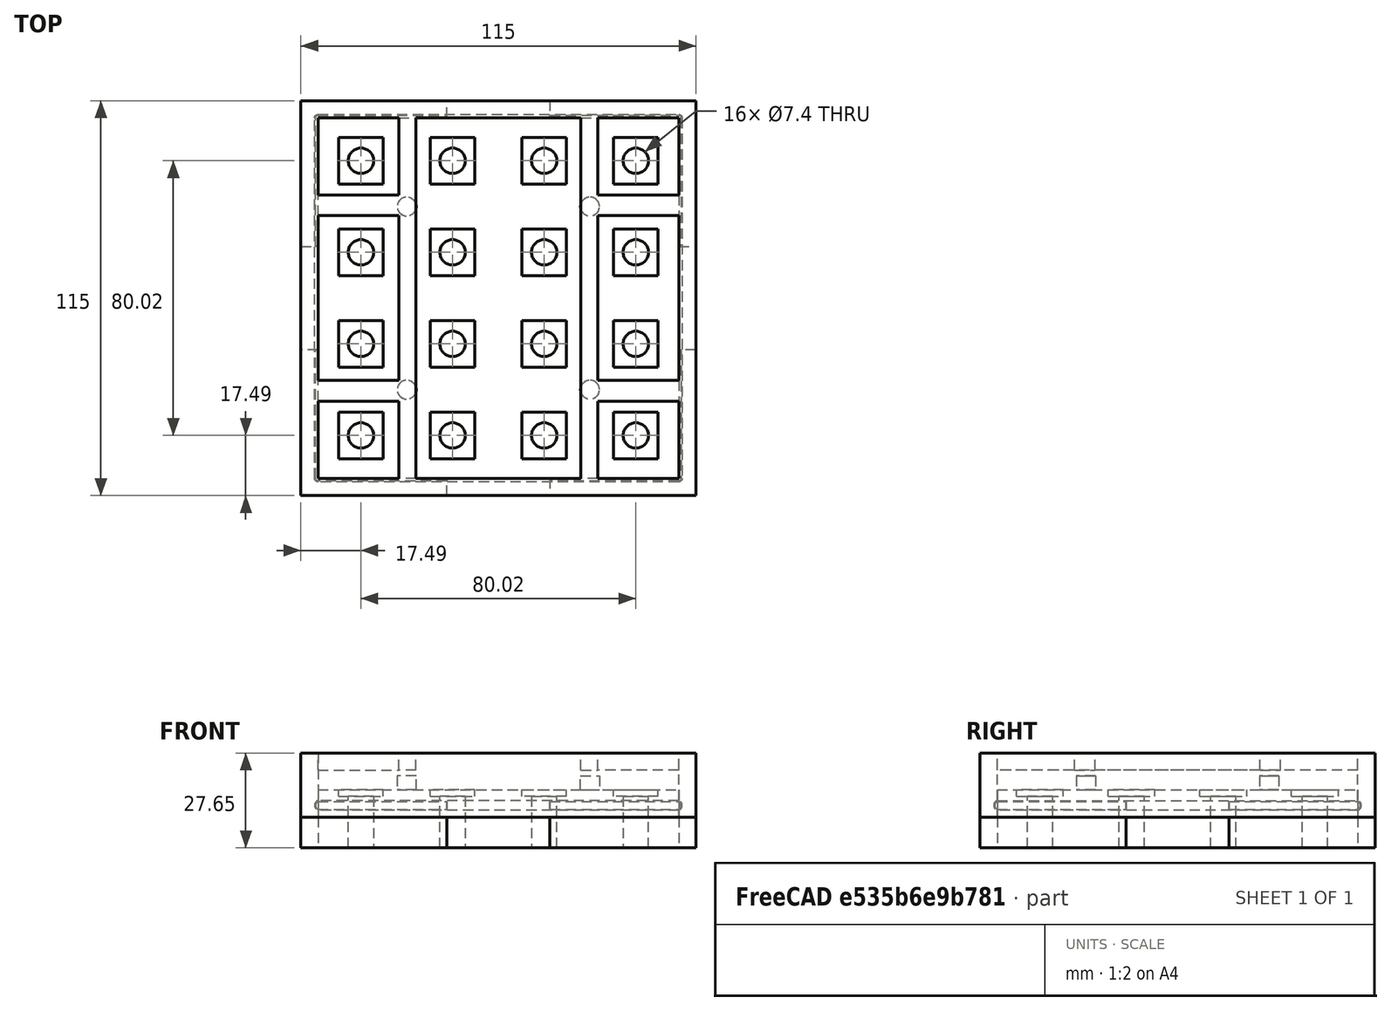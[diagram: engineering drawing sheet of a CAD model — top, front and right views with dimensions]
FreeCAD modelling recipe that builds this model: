
FCSTD DOCUMENT  (FreeCAD 0.21R33668 +26 (Git))
Label: EN16_solder_jig másolata
License: All rights reserved
LicenseURL: https://en.wikipedia.org/wiki/All_rights_reserved
objects: Sketcher::SketchObject×11, PartDesign::Pad×4, PartDesign::Pocket×4, PartDesign::Plane×2, PartDesign::Mirrored×2, PartDesign::Body×2, PartDesign::AdditivePipe×1, PartDesign::SubtractivePipe×1, PartDesign::PolarPattern×1
note: 38 computed .brp shape members not serialized (recipe doc carries the construction recipe); baked Part::Feature solids carry a one-line shape summary decoded from their .brp

FEATURE [Sketcher::SketchObject] Sketch
  FullyConstrained = true
  MapMode = 5
  Support = -> [XY_Plane]
  sketch-geometry (48):
    g0: LineSegment StartX=-46.51 StartY=46.81 StartZ=0 EndX=-46.51 EndY=33.21 EndZ=0
    g1: LineSegment StartX=-46.51 StartY=33.21 StartZ=0 EndX=-33.51 EndY=33.21 EndZ=0
    g2: LineSegment StartX=-33.51 StartY=33.21 StartZ=0 EndX=-33.51 EndY=46.81 EndZ=0
    g3: LineSegment StartX=-33.51 StartY=46.81 StartZ=0 EndX=-46.51 EndY=46.81 EndZ=0
    g4: GeomPoint X=-40.01 Y=40.01 Z=0
    g5: LineSegment StartX=-19.84 StartY=46.81 StartZ=0 EndX=-19.84 EndY=33.21 EndZ=0
    g6: LineSegment StartX=-19.84 StartY=33.21 StartZ=0 EndX=-6.84 EndY=33.21 EndZ=0
    g7: LineSegment StartX=-6.84 StartY=33.21 StartZ=0 EndX=-6.84 EndY=46.81 EndZ=0
    g8: LineSegment StartX=-6.84 StartY=46.81 StartZ=0 EndX=-19.84 EndY=46.81 EndZ=0
    g9: GeomPoint X=-13.34 Y=40.01 Z=0
    g10: LineSegment StartX=-46.51 StartY=20.14 StartZ=0 EndX=-46.51 EndY=6.54 EndZ=0
    g11: LineSegment StartX=-46.51 StartY=6.54 StartZ=0 EndX=-33.51 EndY=6.54 EndZ=0
    g12: LineSegment StartX=-33.51 StartY=6.54 StartZ=0 EndX=-33.51 EndY=20.14 EndZ=0
    g13: LineSegment StartX=-33.51 StartY=20.14 StartZ=0 EndX=-46.51 EndY=20.14 EndZ=0
    g14: GeomPoint X=-40.01 Y=13.34 Z=0
    g15: LineSegment StartX=-19.84 StartY=20.14 StartZ=0 EndX=-19.84 EndY=6.54 EndZ=0
    g16: LineSegment StartX=-19.84 StartY=6.54 StartZ=0 EndX=-6.84 EndY=6.54 EndZ=0
    g17: LineSegment StartX=-6.84 StartY=6.54 StartZ=0 EndX=-6.84 EndY=20.14 EndZ=0
    g18: LineSegment StartX=-6.84 StartY=20.14 StartZ=0 EndX=-19.84 EndY=20.14 EndZ=0
    g19: GeomPoint X=-13.34 Y=13.34 Z=0
    g20: LineSegment StartX=-46.51 StartY=-46.81 StartZ=0 EndX=-46.51 EndY=-33.21 EndZ=0
    g21: LineSegment StartX=-46.51 StartY=-33.21 StartZ=0 EndX=-33.51 EndY=-33.21 EndZ=0
    g22: LineSegment StartX=-33.51 StartY=-33.21 StartZ=0 EndX=-33.51 EndY=-46.81 EndZ=0
    g23: LineSegment StartX=-33.51 StartY=-46.81 StartZ=0 EndX=-46.51 EndY=-46.81 EndZ=0
    g24: GeomPoint X=-40.01 Y=-40.01 Z=0
    g25: LineSegment StartX=-19.84 StartY=-46.81 StartZ=0 EndX=-19.84 EndY=-33.21 EndZ=0
    g26: LineSegment StartX=-19.84 StartY=-33.21 StartZ=0 EndX=-6.84 EndY=-33.21 EndZ=0
    g27: LineSegment StartX=-6.84 StartY=-33.21 StartZ=0 EndX=-6.84 EndY=-46.81 EndZ=0
    g28: LineSegment StartX=-6.84 StartY=-46.81 StartZ=0 EndX=-19.84 EndY=-46.81 EndZ=0
    g29: GeomPoint X=-13.34 Y=-40.01 Z=0
    g30: LineSegment StartX=-46.51 StartY=-20.14 StartZ=0 EndX=-46.51 EndY=-6.54 EndZ=0
    g31: LineSegment StartX=-46.51 StartY=-6.54 StartZ=0 EndX=-33.51 EndY=-6.54 EndZ=0
    g32: LineSegment StartX=-33.51 StartY=-6.54 StartZ=0 EndX=-33.51 EndY=-20.14 EndZ=0
    g33: LineSegment StartX=-33.51 StartY=-20.14 StartZ=0 EndX=-46.51 EndY=-20.14 EndZ=0
    g34: GeomPoint X=-40.01 Y=-13.34 Z=0
    g35: LineSegment StartX=-19.84 StartY=-20.14 StartZ=0 EndX=-19.84 EndY=-6.54 EndZ=0
    g36: LineSegment StartX=-19.84 StartY=-6.54 StartZ=0 EndX=-6.84 EndY=-6.54 EndZ=0
    g37: LineSegment StartX=-6.84 StartY=-6.54 StartZ=0 EndX=-6.84 EndY=-20.14 EndZ=0
    g38: LineSegment StartX=-6.84 StartY=-20.14 StartZ=0 EndX=-19.84 EndY=-20.14 EndZ=0
    g39: GeomPoint X=-13.34 Y=-13.34 Z=0
    g40: LineSegment StartX=-40.01 StartY=40.01 StartZ=0 EndX=-13.34 EndY=40.01 EndZ=0
    g41: LineSegment StartX=-13.34 StartY=40.01 StartZ=0 EndX=-13.34 EndY=13.34 EndZ=0
    g42: LineSegment StartX=-13.34 StartY=13.34 StartZ=0 EndX=-13.34 EndY=0 EndZ=0
    g43: LineSegment StartX=-13.34 StartY=0 StartZ=0 EndX=-13.34 EndY=-13.34 EndZ=0
    g44: LineSegment StartX=-13.34 StartY=-13.34 StartZ=0 EndX=-13.34 EndY=-40.01 EndZ=0
    g45: LineSegment StartX=-13.34 StartY=-13.34 StartZ=0 EndX=-40.01 EndY=-13.34 EndZ=0
    g46: LineSegment StartX=-13.34 StartY=13.34 StartZ=0 EndX=0 EndY=13.34 EndZ=0
    g47: LineSegment StartX=-13.34 StartY=-13.34 StartZ=0 EndX=0 EndY=-13.34 EndZ=0
  constraints (123):
    c: Coincident(g0,g1)
    c: Coincident(g1,g2)
    c: Coincident(g2,g3)
    c: Coincident(g3,g0)
    c: Horizontal(g1)
    c: Horizontal(g3)
    c: Vertical(g0)
    c: Vertical(g2)
    c: Symmetric(g1,g0,g4)
    c: Coincident(g5,g6)
    c: Coincident(g6,g7)
    c: Coincident(g7,g8)
    c: Coincident(g8,g5)
    c: Horizontal(g6)
    c: Horizontal(g8)
    c: Vertical(g5)
    c: Vertical(g7)
    c: Symmetric(g6,g5,g9)
    c: Coincident(g10,g11)
    c: Coincident(g11,g12)
    c: Coincident(g12,g13)
    c: Coincident(g13,g10)
    c: Horizontal(g11)
    c: Horizontal(g13)
    c: Vertical(g10)
    c: Vertical(g12)
    c: Symmetric(g11,g10,g14)
    c: Coincident(g15,g16)
    c: Coincident(g16,g17)
    c: Coincident(g17,g18)
    c: Coincident(g18,g15)
    c: Horizontal(g16)
    c: Horizontal(g18)
    c: Vertical(g15)
    c: Vertical(g17)
    c: Symmetric(g16,g15,g19)
    c: Horizontal(g19,g14)
    c: Horizontal(g9,g4)
    c: Vertical(g9,g19)
    c: Vertical(g4,g14)
    c: Equal(g2,g7)
    c: Equal(g7,g17)
    c: Equal(g17,g12)
    c: Equal(g1,g13)
    c: Equal(g13,g6)
    c: Equal(g6,g18)
    c: DistanceX(g8,g8) = 13
    c: Coincident(g20,g21)
    c: Coincident(g21,g22)
    c: Coincident(g22,g23)
    c: Coincident(g23,g20)
    c: Horizontal(g21)
    c: Horizontal(g23)
    c: Vertical(g20)
    c: Vertical(g22)
    c: Symmetric(g21,g20,g24)
    c: Coincident(g25,g26)
    c: Coincident(g26,g27)
    c: Coincident(g27,g28)
    c: Coincident(g28,g25)
    c: Horizontal(g26)
    c: Horizontal(g28)
    c: Vertical(g25)
    c: Vertical(g27)
    c: Symmetric(g26,g25,g29)
    c: Coincident(g30,g31)
    c: Coincident(g31,g32)
    c: Coincident(g32,g33)
    c: Coincident(g33,g30)
    c: Horizontal(g31)
    c: Horizontal(g33)
    c: Vertical(g30)
    c: Vertical(g32)
    c: Symmetric(g31,g30,g34)
    c: Coincident(g35,g36)
    c: Coincident(g36,g37)
    c: Coincident(g37,g38)
    c: Coincident(g38,g35)
    c: Horizontal(g36)
    c: Horizontal(g38)
    c: Vertical(g35)
    c: Vertical(g37)
    c: Symmetric(g36,g35,g39)
    c: Equal(g22,g27)
    c: Equal(g27,g37)
    c: Equal(g37,g32)
    c: Equal(g21,g33)
    c: Equal(g33,g26)
    c: Equal(g26,g38)
    c: DistanceY(g7,g7) = 13.6
    c: Coincident(g40,g4)
    c: Coincident(g40,g9)
    c: Coincident(g41,g40)
    c: Coincident(g41,g19)
    c: Coincident(g42,g41)
    c: PointOnObject(g42,g-1)
    c: Vertical(g42)
    c: Coincident(g43,g42)
    c: Coincident(g43,g39)
    c: Vertical(g43)
    c: Coincident(g44,g43)
    c: Coincident(g44,g29)
    c: Vertical(g44)
    c: Coincident(g45,g43)
    c: Coincident(g45,g34)
    c: Horizontal(g45)
    c: DistanceY(g41,g41) = 26.67
    c: DistanceX(g40,g40) = 26.67
    c: DistanceY(g42,g42) = 13.34
    c: Coincident(g46,g41)
    c: PointOnObject(g46,g-2)
    c: Horizontal(g46)
    c: DistanceX(g46,g46) = 13.34
    c: Coincident(g47,g43)
    c: PointOnObject(g47,g-2)
    c: Horizontal(g47)
    c: Equal(g42,g43)
    c: Equal(g41,g44)
    c: Equal(g45,g40)
    c: Equal(g32,g12)
    c: Equal(g31,g11)
    c: Horizontal(g24,g44)
    c: Vertical(g24,g45)
FEATURE [Sketcher::SketchObject] Sketch001
  FullyConstrained = true
  MapMode = 5
  Support = -> [XY_Plane]
  sketch-geometry (5):
    g0: LineSegment StartX=-57.5 StartY=57.5 StartZ=0 EndX=-57.5 EndY=-57.5 EndZ=0
    g1: LineSegment StartX=-57.5 StartY=-57.5 StartZ=0 EndX=57.5 EndY=-57.5 EndZ=0
    g2: LineSegment StartX=57.5 StartY=-57.5 StartZ=0 EndX=57.5 EndY=57.5 EndZ=0
    g3: LineSegment StartX=57.5 StartY=57.5 StartZ=0 EndX=-57.5 EndY=57.5 EndZ=0
    g4: GeomPoint X=0 Y=0 Z=0
  constraints (12):
    c: Coincident(g0,g1)
    c: Coincident(g1,g2)
    c: Coincident(g2,g3)
    c: Coincident(g3,g0)
    c: Horizontal(g1)
    c: Horizontal(g3)
    c: Vertical(g0)
    c: Vertical(g2)
    c: Symmetric(g1,g0,g4)
    c: Coincident(g4,g-1)
    c: DistanceY(g2,g2) = 115
    c: Equal(g3,g2)
FEATURE [PartDesign::Pad] Pad
  Direction = (0,0,1)
  Length = 2
  Length2 = 15
  Midplane = true
  Profile = -> Sketch001
  ReferenceAxis = -> Sketch001 [N_Axis]
  Type = 4
FEATURE [Sketcher::SketchObject] Sketch005
  FullyConstrained = true
  MapMode = 5
  Support = -> [XY_Plane]
  sketch-geometry (2):
    g0: Circle CenterX=-26.67 CenterY=26.67 CenterZ=0 NormalX=0 NormalY=0 NormalZ=1 AngleXU=0 Radius=1.25
    g1: Circle CenterX=-26.67 CenterY=-26.67 CenterZ=0 NormalX=0 NormalY=0 NormalZ=1 AngleXU=0 Radius=1.25
  constraints (5):
    c: Equal(g0,g1)
    c: DistanceX(g0,g-1) = 26.67
    c: DistanceY(g1,g0) = 53.34
    c: Symmetric(g1,g0,g-1)
    c: Diameter(g0) = 2.5
FEATURE [PartDesign::Plane] DatumPlane
  AttachmentOffset = pos=(0,0,2) rot=(0,0,1;0rad)
  Length = 138
  MapMode = 5
  Placement = pos=(0,0,2) rot=(0,0,1;0rad)
  ResizeMode = 0
  Support = -> [XY_Plane]
  Width = 138
FEATURE [Sketcher::SketchObject] Sketch002
  FullyConstrained = true
  MapMode = 5
  Placement = pos=(0,0,2) rot=(0,0,1;0rad)
  Support = -> [DatumPlane]
  sketch-geometry (10):
    g0: LineSegment StartX=-52.5 StartY=-52.5 StartZ=0 EndX=-52.5 EndY=52.5 EndZ=0
    g1: LineSegment StartX=-52.5 StartY=52.5 StartZ=0 EndX=52.5 EndY=52.5 EndZ=0
    g2: LineSegment StartX=52.5 StartY=52.5 StartZ=0 EndX=52.5 EndY=-52.5 EndZ=0
    g3: LineSegment StartX=52.5 StartY=-52.5 StartZ=0 EndX=-52.5 EndY=-52.5 EndZ=0
    g4: GeomPoint X=0 Y=0 Z=0
    g5: LineSegment StartX=-57.5 StartY=-57.5 StartZ=0 EndX=-57.5 EndY=57.5 EndZ=0
    g6: LineSegment StartX=-57.5 StartY=57.5 StartZ=0 EndX=57.5 EndY=57.5 EndZ=0
    g7: LineSegment StartX=57.5 StartY=57.5 StartZ=0 EndX=57.5 EndY=-57.5 EndZ=0
    g8: LineSegment StartX=57.5 StartY=-57.5 StartZ=0 EndX=-57.5 EndY=-57.5 EndZ=0
    g9: GeomPoint X=0 Y=0 Z=0
  constraints (24):
    c: Coincident(g0,g1)
    c: Coincident(g1,g2)
    c: Coincident(g2,g3)
    c: Coincident(g3,g0)
    c: Horizontal(g1)
    c: Horizontal(g3)
    c: Vertical(g0)
    c: Vertical(g2)
    c: Symmetric(g1,g0,g4)
    c: Coincident(g4,g-1)
    c: DistanceX(g1,g1) = 105
    c: Equal(g1,g2)
    c: Coincident(g5,g6)
    c: Coincident(g6,g7)
    c: Coincident(g7,g8)
    c: Coincident(g8,g5)
    c: Horizontal(g6)
    c: Horizontal(g8)
    c: Vertical(g5)
    c: Vertical(g7)
    c: Symmetric(g6,g5,g9)
    c: Coincident(g9,g4)
    c: Equal(g7,g6)
    c: DistanceX(g6,g6) = 115
FEATURE [PartDesign::Pocket] Pocket
  BaseFeature = -> Pad
  Direction = (0,0,-1)
  Length = 8
  Length2 = 5
  Profile = -> Sketch002
  ReferenceAxis = -> Sketch002 [N_Axis]
  Type = 0
FEATURE [PartDesign::Pocket] Pocket001
  BaseFeature = -> Pocket
  Direction = (0,0,-1)
  Length = 2.5
  Length2 = 5
  Profile = -> Sketch
  ReferenceAxis = -> Sketch [N_Axis]
  Reversed = true
  Type = 0
FEATURE [Sketcher::SketchObject] Sketch003
  FullyConstrained = true
  MapMode = 5
  Placement = pos=(0,0,2) rot=(0,0,1;0rad)
  Support = -> [DatumPlane]
  sketch-geometry (56):
    g0: LineSegment StartX=-46.31 StartY=46.61 StartZ=0 EndX=-46.31 EndY=33.41 EndZ=0
    g1: LineSegment StartX=-46.31 StartY=33.41 StartZ=0 EndX=-33.71 EndY=33.41 EndZ=0
    g2: LineSegment StartX=-33.71 StartY=33.41 StartZ=0 EndX=-33.71 EndY=46.61 EndZ=0
    g3: LineSegment StartX=-33.71 StartY=46.61 StartZ=0 EndX=-46.31 EndY=46.61 EndZ=0
    g4: GeomPoint X=-40.01 Y=40.01 Z=0
    g5: LineSegment StartX=-19.64 StartY=46.61 StartZ=0 EndX=-19.64 EndY=33.41 EndZ=0
    g6: LineSegment StartX=-19.64 StartY=33.41 StartZ=0 EndX=-7.04 EndY=33.41 EndZ=0
    g7: LineSegment StartX=-7.04 StartY=33.41 StartZ=0 EndX=-7.04 EndY=46.61 EndZ=0
    g8: LineSegment StartX=-7.04 StartY=46.61 StartZ=0 EndX=-19.64 EndY=46.61 EndZ=0
    g9: GeomPoint X=-13.34 Y=40.01 Z=0
    g10: LineSegment StartX=-46.31 StartY=19.94 StartZ=0 EndX=-46.31 EndY=6.74 EndZ=0
    g11: LineSegment StartX=-46.31 StartY=6.74 StartZ=0 EndX=-33.71 EndY=6.74 EndZ=0
    g12: LineSegment StartX=-33.71 StartY=6.74 StartZ=0 EndX=-33.71 EndY=19.94 EndZ=0
    g13: LineSegment StartX=-33.71 StartY=19.94 StartZ=0 EndX=-46.31 EndY=19.94 EndZ=0
    g14: GeomPoint X=-40.01 Y=13.34 Z=0
    g15: LineSegment StartX=-19.64 StartY=19.94 StartZ=0 EndX=-19.64 EndY=6.74 EndZ=0
    g16: LineSegment StartX=-19.64 StartY=6.74 StartZ=0 EndX=-7.04 EndY=6.74 EndZ=0
    g17: LineSegment StartX=-7.04 StartY=6.74 StartZ=0 EndX=-7.04 EndY=19.94 EndZ=0
    g18: LineSegment StartX=-7.04 StartY=19.94 StartZ=0 EndX=-19.64 EndY=19.94 EndZ=0
    g19: GeomPoint X=-13.34 Y=13.34 Z=0
    g20: LineSegment StartX=-46.31 StartY=-46.61 StartZ=0 EndX=-46.31 EndY=-33.41 EndZ=0
    g21: LineSegment StartX=-46.31 StartY=-33.41 StartZ=0 EndX=-33.71 EndY=-33.41 EndZ=0
    g22: LineSegment StartX=-33.71 StartY=-33.41 StartZ=0 EndX=-33.71 EndY=-46.61 EndZ=0
    g23: LineSegment StartX=-33.71 StartY=-46.61 StartZ=0 EndX=-46.31 EndY=-46.61 EndZ=0
    g24: GeomPoint X=-40.01 Y=-40.01 Z=0
    g25: LineSegment StartX=-19.64 StartY=-46.61 StartZ=0 EndX=-19.64 EndY=-33.41 EndZ=0
    g26: LineSegment StartX=-19.64 StartY=-33.41 StartZ=0 EndX=-7.04 EndY=-33.41 EndZ=0
    g27: LineSegment StartX=-7.04 StartY=-33.41 StartZ=0 EndX=-7.04 EndY=-46.61 EndZ=0
    g28: LineSegment StartX=-7.04 StartY=-46.61 StartZ=0 EndX=-19.64 EndY=-46.61 EndZ=0
    g29: GeomPoint X=-13.34 Y=-40.01 Z=0
    g30: LineSegment StartX=-46.31 StartY=-19.94 StartZ=0 EndX=-46.31 EndY=-6.74 EndZ=0
    g31: LineSegment StartX=-46.31 StartY=-6.74 StartZ=0 EndX=-33.71 EndY=-6.74 EndZ=0
    g32: LineSegment StartX=-33.71 StartY=-6.74 StartZ=0 EndX=-33.71 EndY=-19.94 EndZ=0
    g33: LineSegment StartX=-33.71 StartY=-19.94 StartZ=0 EndX=-46.31 EndY=-19.94 EndZ=0
    g34: GeomPoint X=-40.01 Y=-13.34 Z=0
    g35: LineSegment StartX=-19.64 StartY=-19.94 StartZ=0 EndX=-19.64 EndY=-6.74 EndZ=0
    g36: LineSegment StartX=-19.64 StartY=-6.74 StartZ=0 EndX=-7.04 EndY=-6.74 EndZ=0
    g37: LineSegment StartX=-7.04 StartY=-6.74 StartZ=0 EndX=-7.04 EndY=-19.94 EndZ=0
    g38: LineSegment StartX=-7.04 StartY=-19.94 StartZ=0 EndX=-19.64 EndY=-19.94 EndZ=0
    g39: GeomPoint X=-13.34 Y=-13.34 Z=0
    g40: LineSegment StartX=-40.01 StartY=40.01 StartZ=0 EndX=-13.34 EndY=40.01 EndZ=0
    g41: LineSegment StartX=-13.34 StartY=40.01 StartZ=0 EndX=-13.34 EndY=13.34 EndZ=0
    g42: LineSegment StartX=-13.34 StartY=13.34 StartZ=0 EndX=-13.34 EndY=0 EndZ=0
    g43: LineSegment StartX=-13.34 StartY=0 StartZ=0 EndX=-13.34 EndY=-13.34 EndZ=0
    g44: LineSegment StartX=-13.34 StartY=-13.34 StartZ=0 EndX=-13.34 EndY=-40.01 EndZ=0
    g45: LineSegment StartX=-13.34 StartY=-13.34 StartZ=0 EndX=-40.01 EndY=-13.34 EndZ=0
    g46: LineSegment StartX=-13.34 StartY=13.34 StartZ=0 EndX=0 EndY=13.34 EndZ=0
    g47: LineSegment StartX=-13.34 StartY=-13.34 StartZ=0 EndX=0 EndY=-13.34 EndZ=0
    g48: Circle CenterX=-40.01 CenterY=40.01 CenterZ=0 NormalX=0 NormalY=0 NormalZ=1 AngleXU=0 Radius=3.7
    g49: Circle CenterX=-40.01 CenterY=13.34 CenterZ=0 NormalX=0 NormalY=0 NormalZ=1 AngleXU=0 Radius=3.7
    g50: Circle CenterX=-40.01 CenterY=-13.34 CenterZ=0 NormalX=0 NormalY=0 NormalZ=1 AngleXU=0 Radius=3.7
    g51: Circle CenterX=-13.34 CenterY=-13.34 CenterZ=0 NormalX=0 NormalY=0 NormalZ=1 AngleXU=0 Radius=3.7
    g52: Circle CenterX=-13.34 CenterY=-40.01 CenterZ=0 NormalX=0 NormalY=0 NormalZ=1 AngleXU=0 Radius=3.7
    g53: Circle CenterX=-40.01 CenterY=-40.01 CenterZ=0 NormalX=0 NormalY=0 NormalZ=1 AngleXU=0 Radius=3.7
    g54: Circle CenterX=-13.34 CenterY=13.34 CenterZ=0 NormalX=0 NormalY=0 NormalZ=1 AngleXU=0 Radius=3.7
    g55: Circle CenterX=-13.34 CenterY=40.01 CenterZ=0 NormalX=0 NormalY=0 NormalZ=1 AngleXU=0 Radius=3.7
  constraints (139):
    c: Coincident(g0,g1)
    c: Coincident(g1,g2)
    c: Coincident(g2,g3)
    c: Coincident(g3,g0)
    c: Horizontal(g1)
    c: Horizontal(g3)
    c: Vertical(g0)
    c: Vertical(g2)
    c: Symmetric(g1,g0,g4)
    c: Coincident(g5,g6)
    c: Coincident(g6,g7)
    c: Coincident(g7,g8)
    c: Coincident(g8,g5)
    c: Horizontal(g6)
    c: Horizontal(g8)
    c: Vertical(g5)
    c: Vertical(g7)
    c: Symmetric(g6,g5,g9)
    c: Coincident(g10,g11)
    c: Coincident(g11,g12)
    c: Coincident(g12,g13)
    c: Coincident(g13,g10)
    c: Horizontal(g11)
    c: Horizontal(g13)
    c: Vertical(g10)
    c: Vertical(g12)
    c: Symmetric(g11,g10,g14)
    c: Coincident(g15,g16)
    c: Coincident(g16,g17)
    c: Coincident(g17,g18)
    c: Coincident(g18,g15)
    c: Horizontal(g16)
    c: Horizontal(g18)
    c: Vertical(g15)
    c: Vertical(g17)
    c: Symmetric(g16,g15,g19)
    c: Horizontal(g19,g14)
    c: Horizontal(g9,g4)
    c: Vertical(g9,g19)
    c: Vertical(g4,g14)
    c: Equal(g2,g7)
    c: Equal(g7,g17)
    c: Equal(g17,g12)
    c: Equal(g1,g13)
    c: Equal(g13,g6)
    c: Equal(g6,g18)
    c: DistanceX(g8,g8) = 12.6
    c: Coincident(g20,g21)
    c: Coincident(g21,g22)
    c: Coincident(g22,g23)
    c: Coincident(g23,g20)
    c: Horizontal(g21)
    c: Horizontal(g23)
    c: Vertical(g20)
    c: Vertical(g22)
    c: Symmetric(g21,g20,g24)
    c: Coincident(g25,g26)
    c: Coincident(g26,g27)
    c: Coincident(g27,g28)
    c: Coincident(g28,g25)
    c: Horizontal(g26)
    c: Horizontal(g28)
    c: Vertical(g25)
    c: Vertical(g27)
    c: Symmetric(g26,g25,g29)
    c: Coincident(g30,g31)
    c: Coincident(g31,g32)
    c: Coincident(g32,g33)
    c: Coincident(g33,g30)
    c: Horizontal(g31)
    c: Horizontal(g33)
    c: Vertical(g30)
    c: Vertical(g32)
    c: Symmetric(g31,g30,g34)
    c: Coincident(g35,g36)
    c: Coincident(g36,g37)
    c: Coincident(g37,g38)
    c: Coincident(g38,g35)
    c: Horizontal(g36)
    c: Horizontal(g38)
    c: Vertical(g35)
    c: Vertical(g37)
    c: Symmetric(g36,g35,g39)
    c: Equal(g22,g27)
    c: Equal(g27,g37)
    c: Equal(g37,g32)
    c: Equal(g21,g33)
    c: Equal(g33,g26)
    c: Equal(g26,g38)
    c: DistanceY(g7,g7) = 13.2
    c: Coincident(g40,g4)
    c: Coincident(g40,g9)
    c: Coincident(g41,g40)
    c: Coincident(g41,g19)
    c: Coincident(g42,g41)
    c: PointOnObject(g42,g-1)
    c: Vertical(g42)
    c: Coincident(g43,g42)
    c: Coincident(g43,g39)
    c: Vertical(g43)
    c: Coincident(g44,g43)
    c: Coincident(g44,g29)
    c: Vertical(g44)
    c: Coincident(g45,g43)
    c: Coincident(g45,g34)
    c: Horizontal(g45)
    c: DistanceY(g41,g41) = 26.67
    c: DistanceX(g40,g40) = 26.67
    c: DistanceY(g42,g42) = 13.34
    c: Coincident(g46,g41)
    c: PointOnObject(g46,g-2)
    c: Horizontal(g46)
    c: DistanceX(g46,g46) = 13.34
    c: Coincident(g47,g43)
    c: PointOnObject(g47,g-2)
    c: Horizontal(g47)
    c: Equal(g42,g43)
    c: Equal(g41,g44)
    c: Equal(g45,g40)
    c: Equal(g32,g12)
    c: Equal(g31,g11)
    c: Horizontal(g24,g44)
    c: Vertical(g24,g45)
    c: Coincident(g48,g4)
    c: Coincident(g49,g14)
    c: Coincident(g50,g34)
    c: Coincident(g51,g39)
    c: Coincident(g52,g29)
    c: Coincident(g53,g24)
    c: Coincident(g54,g19)
    c: Coincident(g55,g9)
    c: Equal(g48,g55)
    c: Equal(g55,g54)
    c: Equal(g54,g49)
    c: Equal(g49,g51)
    c: Equal(g51,g50)
    c: Equal(g50,g53)
    c: Equal(g53,g52)
    c: Diameter(g48) = 7.4
FEATURE [PartDesign::Pocket] Pocket002
  BaseFeature = -> Pocket001
  Direction = (0,0,-1)
  Length = 5
  Length2 = 5
  Profile = -> Sketch003
  ReferenceAxis = -> Sketch003 [N_Axis]
  Type = 1
FEATURE [Sketcher::SketchObject] Sketch004
  FullyConstrained = true
  MapMode = 5
  Placement = pos=(0,0,2) rot=(0,0,1;0rad)
  Support = -> [DatumPlane]
  sketch-geometry (2):
    g0: Circle CenterX=-26.67 CenterY=26.67 CenterZ=0 NormalX=0 NormalY=0 NormalZ=1 AngleXU=0 Radius=2.75
    g1: Circle CenterX=-26.67 CenterY=-26.67 CenterZ=0 NormalX=0 NormalY=0 NormalZ=1 AngleXU=0 Radius=2.75
  constraints (5):
    c: DistanceY(g1,g0) = 53.34
    c: Equal(g0,g1)
    c: Diameter(g0) = 5.5
    c: Symmetric(g0,g1,g-1)
    c: DistanceX(g0,g-1) = 26.67
FEATURE [PartDesign::Pad] Pad001
  BaseFeature = -> Pocket002
  Direction = (0,0,1)
  Length = 4
  Length2 = 10
  Profile = -> Sketch004
  ReferenceAxis = -> Sketch004 [N_Axis]
  Type = 0
FEATURE [PartDesign::Mirrored] Mirrored
  BaseFeature = -> Pad001
  MirrorPlane = -> Sketch [V_Axis]
  Originals = -> [Pocket001,Pocket002,Pad001]
FEATURE [PartDesign::Plane] DatumPlane001
  AttachmentOffset = pos=(0,0,7.65) rot=(0,0,1;0rad)
  Length = 138
  MapMode = 5
  Placement = pos=(0,0,7.65) rot=(0,0,1;0rad)
  ResizeMode = 0
  Support = -> [XY_Plane003]
  Width = 138
FEATURE [Sketcher::SketchObject] Sketch006
  FullyConstrained = true
  MapMode = 5
  Placement = pos=(0,0,7.65) rot=(0,0,1;0rad)
  Support = -> [DatumPlane001]
  sketch-geometry (22):
    g0: LineSegment StartX=-57.5 StartY=-57.5 StartZ=0 EndX=-57.5 EndY=57.5 EndZ=0
    g1: LineSegment StartX=-57.5 StartY=57.5 StartZ=0 EndX=0 EndY=57.5 EndZ=0
    g2: LineSegment StartX=0 StartY=-57.5 StartZ=0 EndX=-57.5 EndY=-57.5 EndZ=0
    g3: GeomPoint X=0 Y=0 Z=0
    g4: LineSegment StartX=-52.5 StartY=-52.5 StartZ=0 EndX=-52.5 EndY=-30 EndZ=0
    g5: LineSegment StartX=-52.5 StartY=52.5 StartZ=0 EndX=-29 EndY=52.5 EndZ=0
    g6: LineSegment StartX=0 StartY=-52.5 StartZ=0 EndX=-24 EndY=-52.5 EndZ=0
    g7: GeomPoint X=0 Y=0 Z=0
    g8: LineSegment StartX=0 StartY=57.5 StartZ=0 EndX=0 EndY=52.5 EndZ=0
    g9: LineSegment StartX=0 StartY=-52.5 StartZ=0 EndX=0 EndY=-57.5 EndZ=0
    g10: LineSegment StartX=-29 StartY=52.5 StartZ=0 EndX=-29 EndY=30 EndZ=0
    g11: LineSegment StartX=-24 StartY=52.5 StartZ=0 EndX=-24 EndY=-52.5 EndZ=0
    g12: LineSegment StartX=-52.5 StartY=-30 StartZ=0 EndX=-29 EndY=-30 EndZ=0
    g13: LineSegment StartX=-52.5 StartY=-24 StartZ=0 EndX=-29 EndY=-24 EndZ=0
    g14: LineSegment StartX=-52.5 StartY=30 StartZ=0 EndX=-29 EndY=30 EndZ=0
    g15: LineSegment StartX=-52.5 StartY=24 StartZ=0 EndX=-29 EndY=24 EndZ=0
    g16: LineSegment StartX=-29 StartY=24 StartZ=0 EndX=-29 EndY=-24 EndZ=0
    g17: LineSegment StartX=-29 StartY=-30 StartZ=0 EndX=-29 EndY=-52.5 EndZ=0
    g18: LineSegment StartX=-52.5 StartY=30 StartZ=0 EndX=-52.5 EndY=52.5 EndZ=0
    g19: LineSegment StartX=-52.5 StartY=-24 StartZ=0 EndX=-52.5 EndY=24 EndZ=0
    g20: LineSegment StartX=-24 StartY=52.5 StartZ=0 EndX=0 EndY=52.5 EndZ=0
    g21: LineSegment StartX=-29 StartY=-52.5 StartZ=0 EndX=-52.5 EndY=-52.5 EndZ=0
  constraints (59):
    c: Coincident(g0,g1)
    c: Coincident(g2,g0)
    c: Horizontal(g1)
    c: Horizontal(g2)
    c: Vertical(g0)
    c: Coincident(g3,g-1)
    c: Coincident(g18,g5)
    c: Coincident(g21,g4)
    c: Horizontal(g5)
    c: Horizontal(g6)
    c: Vertical(g4)
    c: Coincident(g7,g3)
    c: Vertical(g8)
    c: Coincident(g1,g8)
    c: Coincident(g2,g9)
    c: Coincident(g8,g20)
    c: Coincident(g9,g6)
    c: DistanceX(g1,g1) = 57.5
    c: DistanceX(g5,g20) = 52.5
    c: Symmetric(g20,g6,g3)
    c: DistanceY(g0,g0) = 115
    c: Symmetric(g2,g1,g3)
    c: DistanceY(g4,g18) = 105
    c: PointOnObject(g6,g-2)
    c: Vertical(g10)
    c: Vertical(g11)
    c: Horizontal(g12)
    c: PointOnObject(g13,g10)
    c: Horizontal(g13)
    c: Horizontal(g14)
    c: Horizontal(g15)
    c: Coincident(g10,g14)
    c: Coincident(g16,g15)
    c: PointOnObject(g16,g13)
    c: Symmetric(g13,g15,g-1)
    c: Coincident(g19,g15)
    c: Coincident(g18,g14)
    c: Coincident(g4,g12)
    c: Coincident(g19,g13)
    c: Vertical(g16)
    c: Vertical(g17)
    c: Coincident(g12,g17)
    c: Symmetric(g10,g12,g-1)
    c: DistanceY(g19,g19) = 48
    c: DistanceY(g15,g14) = 6
    c: DistanceX(g10,g11) = 5
    c: DistanceX(g11,g20) = 24
    c: Vertical(g18)
    c: Vertical(g19)
    c: Vertical(g13,g4)
    c: Vertical(g15,g14)
    c: Coincident(g5,g10)
    c: Coincident(g20,g11)
    c: Coincident(g6,g11)
    c: Coincident(g21,g17)
    c: Horizontal(g20)
    c: Horizontal(g21)
    c: Horizontal(g6,g17)
    c: Horizontal(g5,g11)
FEATURE [PartDesign::Pad] Pad002
  Direction = (0,0,1)
  Length = 5
  Length2 = 10
  Placement = pos=(0,0,7.65) rot=(0,0,1;0rad)
  Profile = -> Sketch006
  ReferenceAxis = -> Sketch006 [N_Axis]
  Type = 0
FEATURE [Sketcher::SketchObject] Sketch007
  FullyConstrained = true
  MapMode = 5
  Placement = pos=(0,0,7.65) rot=(0,0,1;0rad)
  Support = -> [DatumPlane001]
  sketch-geometry (8):
    g0: LineSegment StartX=0 StartY=57.5 StartZ=0 EndX=-57.5 EndY=57.5 EndZ=0
    g1: LineSegment StartX=-57.5 StartY=57.5 StartZ=0 EndX=-57.5 EndY=-57.5 EndZ=0
    g2: LineSegment StartX=-57.5 StartY=-57.5 StartZ=0 EndX=0 EndY=-57.5 EndZ=0
    g3: LineSegment StartX=0 StartY=-57.5 StartZ=0 EndX=0 EndY=-52.5 EndZ=0
    g4: LineSegment StartX=0 StartY=-52.5 StartZ=0 EndX=-52.5 EndY=-52.5 EndZ=0
    g5: LineSegment StartX=-52.5 StartY=-52.5 StartZ=0 EndX=-52.5 EndY=52.5 EndZ=0
    g6: LineSegment StartX=-52.5 StartY=52.5 StartZ=0 EndX=6.395e-13 EndY=52.5 EndZ=0
    g7: LineSegment StartX=6.395e-13 StartY=52.5 StartZ=0 EndX=0 EndY=57.5 EndZ=0
  constraints (22):
    c: PointOnObject(g0,g-2)
    c: Horizontal(g0)
    c: Coincident(g1,g0)
    c: Vertical(g1)
    c: Coincident(g2,g1)
    c: Horizontal(g2)
    c: Coincident(g3,g2)
    c: PointOnObject(g3,g-2)
    c: Coincident(g4,g3)
    c: Horizontal(g4)
    c: Coincident(g5,g4)
    c: Vertical(g5)
    c: Coincident(g6,g5)
    c: Horizontal(g6)
    c: Coincident(g7,g6)
    c: Coincident(g7,g0)
    c: Symmetric(g6,g3,g-1)
    c: Symmetric(g0,g2,g-1)
    c: DistanceY(g1,g1) = 115
    c: DistanceY(g5,g5) = 105
    c: DistanceX(g0,g0) = 57.5
    c: DistanceX(g6,g6) = 52.5
FEATURE [PartDesign::Pad] Pad003
  BaseFeature = -> Pad002
  Direction = (0,0,1)
  Length = 13.65
  Length2 = 10
  Placement = pos=(0,0,7.65) rot=(0,0,1;0rad)
  Profile = -> Sketch007
  ReferenceAxis = -> Sketch007 [N_Axis]
  Refine = true
  Reversed = true
  Type = 0
FEATURE [PartDesign::Mirrored] Mirrored001
  BaseFeature = -> Pad003
  MirrorPlane = -> Sketch007 [V_Axis]
  Originals = -> [Pad003,Pad002]
  Placement = pos=(0,0,7.65) rot=(0,0,1;0rad)
  Refine = true
FEATURE [Sketcher::SketchObject] Sketch008
  FullyConstrained = true
  MapMode = 5
  Placement = pos=(0,0,0) rot=(1,0,0;1.5708rad)
  Support = -> [XZ_Plane]
  sketch-geometry (1):
    g0: Circle CenterX=-52 CenterY=-2.6 CenterZ=0 NormalX=0 NormalY=0 NormalZ=1 AngleXU=0 Radius=1.25
  constraints (3):
    c: DistanceY(g0,g-1) = 2.6
    c: Diameter(g0) = 2.5
    c: DistanceX(g0,g-1) = 52
FEATURE [PartDesign::AdditivePipe] AdditivePipe
  AuxilleryCurvelinear = true
  AuxillerySpineTangent = false
  BaseFeature = -> Mirrored
  Binormal = (0,0,0)
  Mode = 0
  Profile = -> Sketch008
  Spine = -> Mirrored [Edge67,Edge72,Edge71,Edge69]
  SpineTangent = false
  Transformation = 0
  Transition = 2
FEATURE [Sketcher::SketchObject] Sketch009
  FullyConstrained = true
  MapMode = 5
  Placement = pos=(0,0,0) rot=(1,0,0;1.5708rad)
  Support = -> [XZ_Plane003]
  sketch-geometry (1):
    g0: Circle CenterX=-52 CenterY=-2.6 CenterZ=0 NormalX=0 NormalY=0 NormalZ=1 AngleXU=0 Radius=1.5
  constraints (3):
    c: DistanceY(g0,g-1) = 2.6
    c: Diameter(g0) = 3
    c: DistanceX(g0,g-1) = 52
FEATURE [PartDesign::SubtractivePipe] SubtractivePipe
  AuxilleryCurvelinear = true
  AuxillerySpineTangent = false
  BaseFeature = -> Mirrored001
  Binormal = (0,0,0)
  Mode = 0
  Placement = pos=(0,0,7.65) rot=(0,0,1;0rad)
  Profile = -> Sketch009
  Spine = -> Mirrored001 [Edge74,Edge94,Edge93,Edge92]
  SpineTangent = false
  Transformation = 0
  Transition = 2
FEATURE [PartDesign::Body] Body003
  Group = -> [DatumPlane001,Sketch006,Pad002,Sketch007,Pad003,Mirrored001,Sketch009,SubtractivePipe]
  Origin = -> Origin003
  Tip = -> SubtractivePipe
FEATURE [Sketcher::SketchObject] Sketch010
  FullyConstrained = true
  MapMode = 5
  Support = -> [XY_Plane]
  sketch-geometry (5):
    g0: LineSegment StartX=-15 StartY=52.5 StartZ=0 EndX=-15 EndY=57.5 EndZ=0
    g1: LineSegment StartX=-15 StartY=57.5 StartZ=0 EndX=15 EndY=57.5 EndZ=0
    g2: LineSegment StartX=15 StartY=57.5 StartZ=0 EndX=15 EndY=52.5 EndZ=0
    g3: LineSegment StartX=15 StartY=52.5 StartZ=0 EndX=-15 EndY=52.5 EndZ=0
    g4: GeomPoint X=-1e-16 Y=55 Z=0
  constraints (13):
    c: Coincident(g0,g1)
    c: Coincident(g1,g2)
    c: Coincident(g2,g3)
    c: Coincident(g3,g0)
    c: Horizontal(g1)
    c: Horizontal(g3)
    c: Vertical(g0)
    c: Vertical(g2)
    c: Symmetric(g1,g0,g4)
    c: PointOnObject(g4,g-2)
    c: DistanceY(g-1,g1) = 57.5
    c: DistanceY(g2,g2) = 5
    c: DistanceX(g1,g1) = 30
FEATURE [PartDesign::Pocket] Pocket003
  BaseFeature = -> AdditivePipe
  Direction = (0,0,-1)
  Length = 5
  Length2 = 5
  Profile = -> Sketch010
  ReferenceAxis = -> Sketch010 [N_Axis]
  Refine = true
  Type = 1
FEATURE [PartDesign::PolarPattern] PolarPattern
  Angle = 360
  Axis = -> Sketch010 [N_Axis]
  BaseFeature = -> Pocket003
  Occurrences = 4
  Originals = -> [Pocket003]
  Refine = true
FEATURE [PartDesign::Body] Body
  Group = -> [DatumPlane,Sketch001,Pad,Sketch002,Pocket,Sketch,Pocket001,Sketch003,Pocket002,Sketch004,Pad001,Mirrored,Sketch005,Sketch008,AdditivePipe,Sketch010,Pocket003,PolarPattern]
  Origin = -> Origin
  Tip = -> PolarPattern
